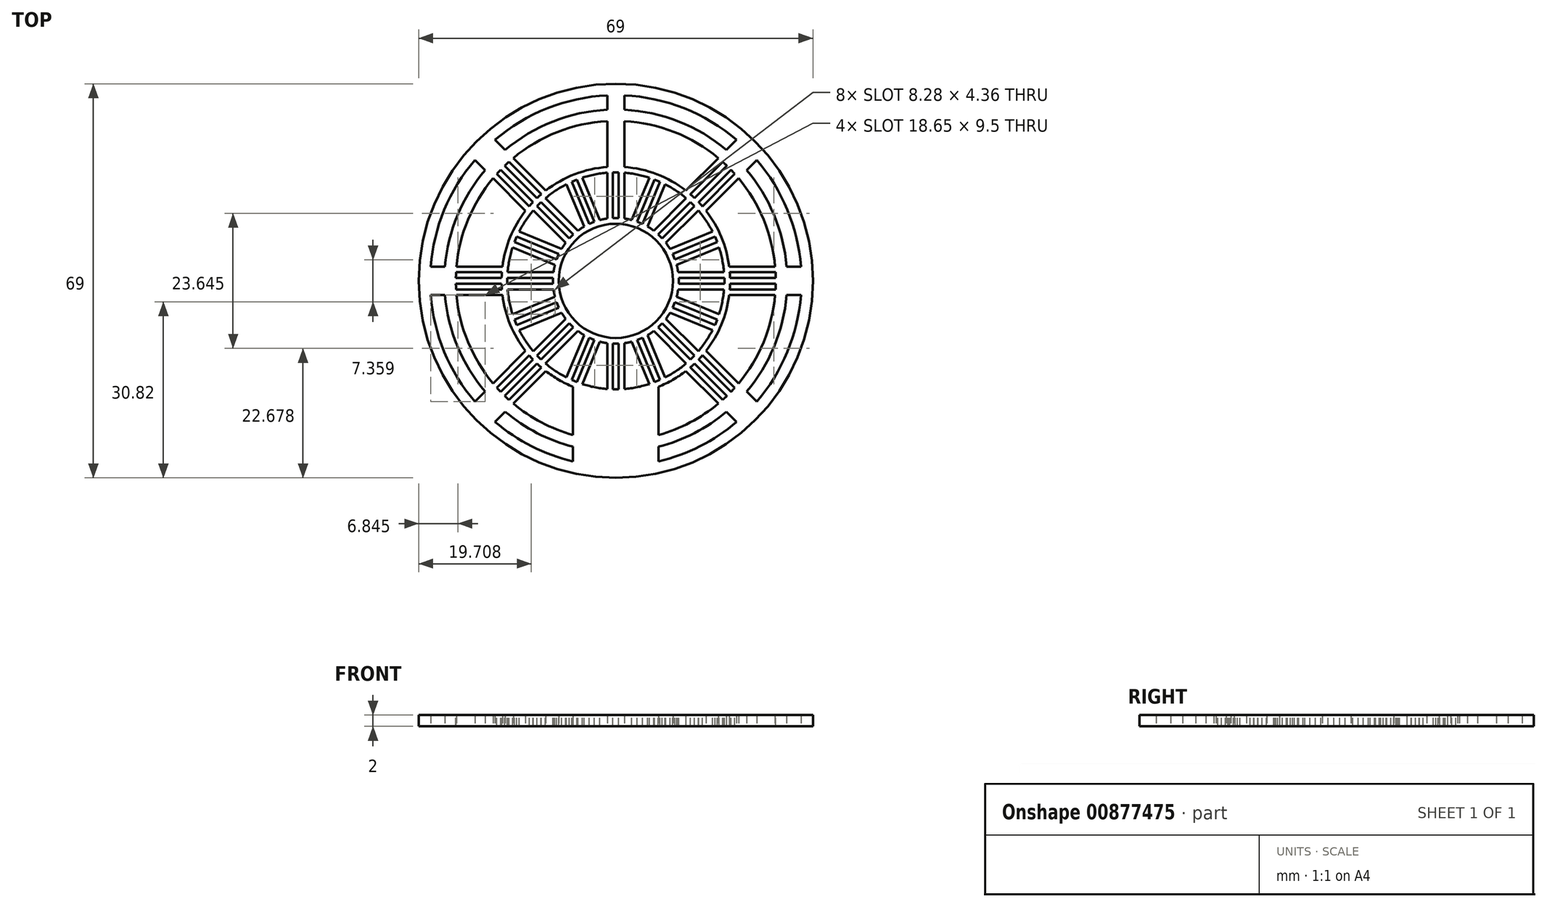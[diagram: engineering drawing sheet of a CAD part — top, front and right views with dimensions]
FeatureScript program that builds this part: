
annotation { "Feature Type Name" : "Feature", "Feature Type Description" : "" }
export const myFeature = defineFeature(function(context is Context, id is Id, definition is map)
    precondition{}
    {
        {
            var Q0;
            Q0=qCreatedBy(makeId("Top.planeOp"),FACE);
            var sketch = newSketch(context, id + "F0", { "sketchPlane" : qUnion([Q0])});
            skLineSegment(sketch, "E0", {"start": v(0, 41.56) * mm, "end": v(0, -42.56) * mm, "construction": true});
            skLineSegment(sketch, "E1", {"start": v(-1.5, 29.96) * mm, "end": v(-1.5, 19.94) * mm});
            skLineSegment(sketch, "E2.MirrorCS", {"start": v(1.5, 29.96) * mm, "end": v(1.5, 19.94) * mm});
            skCircle(sketch, "E3", {"center": v(0, 0) * mm, "radius": 10 * mm});
            skArc(sketch, "E4.trimOffspring", {"start": v(0, 30) * mm, "mid": v(-0.75, 30) * mm, "end": v(-1.5, 29.96) * mm});
            skArc(sketch, "E5", {"start": v(-1.5, 19.94) * mm, "mid": v(-7.19, 18.66) * mm, "end": v(-12.26, 15.8) * mm});
            skArc(sketch, "E6.trimOffspring", {"start": v(7.5, -18.54) * mm, "mid": v(9.98, -17.33) * mm, "end": v(12.26, -15.8) * mm});
            skLineSegment(sketch, "E7", {"start": v(-43.12, 0) * mm, "end": v(49.9, 0) * mm, "construction": true});
            skArc(sketch, "E8.trimOffspring", {"start": v(-19.6, -4) * mm, "mid": v(-18.17, -8.35) * mm, "end": v(-15.8, -12.26) * mm});
            skArc(sketch, "E9.trimOffspring", {"start": v(19.6, 4) * mm, "mid": v(18.17, 8.35) * mm, "end": v(15.8, 12.26) * mm});
            skArc(sketch, "E10", {"start": v(-19.6, 4) * mm, "mid": v(-19.73, 3.25) * mm, "end": v(-19.84, 2.5) * mm});
            skArc(sketch, "E11.trimOffspring", {"start": v(19.6, -4) * mm, "mid": v(19.73, -3.25) * mm, "end": v(19.84, -2.5) * mm});
            skLineSegment(sketch, "E12", {"start": v(-19.84, 2.5) * mm, "end": v(-29.9, 2.5) * mm});
            skLineSegment(sketch, "E13", {"start": v(-19.84, -2.5) * mm, "end": v(-29.9, -2.5) * mm});
            skArc(sketch, "E14.trimOffspring", {"start": v(-19.84, -2.5) * mm, "mid": v(-19.73, -3.25) * mm, "end": v(-19.6, -4) * mm});
            skLineSegment(sketch, "E15.MirrorCS", {"start": v(19.84, 2.5) * mm, "end": v(29.9, 2.5) * mm});
            skLineSegment(sketch, "E16.MirrorCS", {"start": v(19.84, -2.5) * mm, "end": v(29.9, -2.5) * mm});
            skArc(sketch, "E17.trimOffspring", {"start": v(19.84, 2.5) * mm, "mid": v(19.73, 3.25) * mm, "end": v(19.6, 4) * mm});
            skLineSegment(sketch, "E18", {"start": v(-7.5, -18.54) * mm, "end": v(-7.5, -29.05) * mm});
            skLineSegment(sketch, "E19", {"start": v(7.5, -18.54) * mm, "end": v(7.5, -29.05) * mm});
            skArc(sketch, "E20.trimOffspring", {"start": v(1.5, 29.96) * mm, "mid": v(0.75, 30) * mm, "end": v(0, 30) * mm});
            skPoint(sketch, "E21.orphan", {"position": v(29.9, 2.5) * mm});
            skPoint(sketch, "E22.MirrorCS.end.orphan", {"position": v(29.9, -2.5) * mm});
            skArc(sketch, "E23", {"start": v(-19.37, 22.9) * mm, "mid": v(-21.21, 21.21) * mm, "end": v(-22.9, 19.37) * mm});
            skLineSegment(sketch, "E24", {"start": v(-23.88, 23.88) * mm, "end": v(0, 0) * mm, "construction": true});
            skLineSegment(sketch, "E25", {"start": v(-12.26, 15.8) * mm, "end": v(-19.37, 22.9) * mm});
            skLineSegment(sketch, "E26", {"start": v(-15.8, 12.26) * mm, "end": v(-22.9, 19.37) * mm});
            skArc(sketch, "E27.trimOffspring", {"start": v(-29.9, 2.5) * mm, "mid": v(-30, 0) * mm, "end": v(-29.9, -2.5) * mm});
            skArc(sketch, "E28.trimOffspring", {"start": v(-7.5, -29.05) * mm, "mid": v(0, -30) * mm, "end": v(7.5, -29.05) * mm});
            skArc(sketch, "E29.trimOffspring", {"start": v(29.9, -2.5) * mm, "mid": v(30, 0) * mm, "end": v(29.9, 2.5) * mm});
            skArc(sketch, "E30.trimOffspring", {"start": v(1.5, 29.96) * mm, "mid": v(0, 30) * mm, "end": v(-1.5, 29.96) * mm});
            skArc(sketch, "E31.trimOffspring", {"start": v(-15.8, 12.26) * mm, "mid": v(-18.17, 8.35) * mm, "end": v(-19.6, 4) * mm});
            skLineSegment(sketch, "E32.MirrorCS", {"start": v(-15.8, -12.26) * mm, "end": v(-22.9, -19.37) * mm});
            skLineSegment(sketch, "E33.MirrorCS", {"start": v(-12.26, -15.8) * mm, "end": v(-19.37, -22.9) * mm});
            skArc(sketch, "E34.MirrorCS", {"start": v(-19.37, -22.9) * mm, "mid": v(-21.21, -21.21) * mm, "end": v(-22.9, -19.37) * mm});
            skArc(sketch, "E35.MirrorCS", {"start": v(19.37, 22.9) * mm, "mid": v(21.21, 21.21) * mm, "end": v(22.9, 19.37) * mm});
            skLineSegment(sketch, "E36.MirrorCS", {"start": v(12.26, 15.8) * mm, "end": v(19.37, 22.9) * mm});
            skLineSegment(sketch, "E37.MirrorCS", {"start": v(15.8, 12.26) * mm, "end": v(22.9, 19.37) * mm});
            skLineSegment(sketch, "E38.MirrorCS", {"start": v(15.8, -12.26) * mm, "end": v(22.9, -19.37) * mm});
            skArc(sketch, "E39.MirrorCS", {"start": v(19.37, -22.9) * mm, "mid": v(21.21, -21.21) * mm, "end": v(22.9, -19.37) * mm});
            skLineSegment(sketch, "E40.MirrorCS", {"start": v(12.26, -15.8) * mm, "end": v(19.37, -22.9) * mm});
            skArc(sketch, "E41.trimOffspring", {"start": v(12.26, 15.8) * mm, "mid": v(7.19, 18.66) * mm, "end": v(1.5, 19.94) * mm});
            skArc(sketch, "E42.trimOffspring", {"start": v(15.8, -12.26) * mm, "mid": v(18.17, -8.35) * mm, "end": v(19.6, -4) * mm});
            skArc(sketch, "E43.trimOffspring", {"start": v(-12.26, -15.8) * mm, "mid": v(-9.98, -17.33) * mm, "end": v(-7.5, -18.54) * mm});
            skSolve(sketch);
        }
        {
            var Q0;
            Q0=qSketchRegion(id+"F0",true);
            extrude(context, id + "F1", {"entities" : qUnion([Q0]), "depth" : 2 * mm, "offsetDistance" : 25 * mm});
        }
        {
            var Q0;
            Q0=makeQuery(id+"F1.opExtrude","CAP_FACE",FACE,{"disambiguationData":[OSD([sQuery(id+"F0.wireOp",EDGE,"E1"),sQuery(id+"F0.wireOp",EDGE,"E2.MirrorCS"),sQuery(id+"F0.wireOp",EDGE,"AAyOunAg-4wrl-KSGf-zJpX-W6BoPU9CkmaY"),sQuery(id+"F0.wireOp",EDGE,"E3"),sQuery(id+"F0.wireOp",EDGE,"E4.trimOffspring"),sQuery(id+"F0.wireOp",EDGE,"E5"),sQuery(id+"F0.wireOp",EDGE,"c113f9d6-7eb6-46a0-945d-8de39da3101e.trimOffspring"),sQuery(id+"F0.wireOp",EDGE,"3f556c1b-9434-4d6c-9e8b-53cfe23b14e8.trimOffspring"),sQuery(id+"F0.wireOp",EDGE,"E6.trimOffspring"),sQuery(id+"F0.wireOp",EDGE,"E8.trimOffspring"),sQuery(id+"F0.wireOp",EDGE,"E9.trimOffspring"),sQuery(id+"F0.wireOp",EDGE,"E10"),sQuery(id+"F0.wireOp",EDGE,"E11.trimOffspring")])],"isStart":false});
            var sketch = newSketch(context, id + "F2", { "sketchPlane" : qUnion([Q0])});
            skLineSegment(sketch, "E44", {"start": v(0, 19.87) * mm, "end": v(0, -17.42) * mm, "construction": true});
            skLineSegment(sketch, "E45", {"start": v(-0.5, 19) * mm, "end": v(-0.5, 11) * mm});
            skLineSegment(sketch, "E46", {"start": v(-0.5, 11) * mm, "end": v(0, 11) * mm});
            skLineSegment(sketch, "E47", {"start": v(-0.5, 19) * mm, "end": v(0, 19) * mm});
            skCircle(sketch, "E48", {"center": v(0, 0) * mm, "radius": 15 * mm, "construction": true});
            skLineSegment(sketch, "E49.MirrorCS", {"start": v(0.5, 19) * mm, "end": v(0, 19) * mm});
            skLineSegment(sketch, "E50.MirrorCS", {"start": v(0.5, 19) * mm, "end": v(0.5, 11) * mm});
            skLineSegment(sketch, "E51.MirrorCS", {"start": v(0.5, 11) * mm, "end": v(0, 11) * mm});
            skLineSegment(sketch, "E52.1.0", {"start": v(7.73, 17.36) * mm, "end": v(7.27, 17.55) * mm});
            skLineSegment(sketch, "E52.1.1", {"start": v(7.73, 17.36) * mm, "end": v(4.67, 9.97) * mm});
            skLineSegment(sketch, "E52.1.2", {"start": v(6.8, 17.75) * mm, "end": v(7.27, 17.55) * mm});
            skLineSegment(sketch, "E52.1.3", {"start": v(6.8, 17.75) * mm, "end": v(3.75, 10.35) * mm});
            skLineSegment(sketch, "E52.1.4", {"start": v(3.75, 10.35) * mm, "end": v(4.2, 10.16) * mm});
            skLineSegment(sketch, "E52.1.5", {"start": v(4.67, 9.97) * mm, "end": v(4.2, 10.16) * mm});
            skLineSegment(sketch, "E52.2.0", {"start": v(13.79, 13.08) * mm, "end": v(13.44, 13.44) * mm});
            skLineSegment(sketch, "E52.2.1", {"start": v(13.79, 13.08) * mm, "end": v(8.13, 7.42) * mm});
            skLineSegment(sketch, "E52.2.2", {"start": v(13.08, 13.79) * mm, "end": v(13.44, 13.44) * mm});
            skLineSegment(sketch, "E52.2.3", {"start": v(13.08, 13.79) * mm, "end": v(7.42, 8.13) * mm});
            skLineSegment(sketch, "E52.2.4", {"start": v(7.42, 8.13) * mm, "end": v(7.78, 7.78) * mm});
            skLineSegment(sketch, "E52.2.5", {"start": v(8.13, 7.42) * mm, "end": v(7.78, 7.78) * mm});
            skLineSegment(sketch, "E52.3.0", {"start": v(17.75, 6.8) * mm, "end": v(17.55, 7.27) * mm});
            skLineSegment(sketch, "E52.3.1", {"start": v(17.75, 6.8) * mm, "end": v(10.35, 3.75) * mm});
            skLineSegment(sketch, "E52.3.2", {"start": v(17.36, 7.73) * mm, "end": v(17.55, 7.27) * mm});
            skLineSegment(sketch, "E52.3.3", {"start": v(17.36, 7.73) * mm, "end": v(9.97, 4.67) * mm});
            skLineSegment(sketch, "E52.3.4", {"start": v(9.97, 4.67) * mm, "end": v(10.16, 4.2) * mm});
            skLineSegment(sketch, "E52.3.5", {"start": v(10.35, 3.75) * mm, "end": v(10.16, 4.2) * mm});
            skLineSegment(sketch, "E52.4.0", {"start": v(19, -0.5) * mm, "end": v(19, 0) * mm});
            skLineSegment(sketch, "E52.4.1", {"start": v(19, -0.5) * mm, "end": v(11, -0.5) * mm});
            skLineSegment(sketch, "E52.4.2", {"start": v(19, 0.5) * mm, "end": v(19, 0) * mm});
            skLineSegment(sketch, "E52.4.3", {"start": v(19, 0.5) * mm, "end": v(11, 0.5) * mm});
            skLineSegment(sketch, "E52.4.4", {"start": v(11, 0.5) * mm, "end": v(11, 0) * mm});
            skLineSegment(sketch, "E52.4.5", {"start": v(11, -0.5) * mm, "end": v(11, 0) * mm});
            skLineSegment(sketch, "E52.5.0", {"start": v(17.36, -7.73) * mm, "end": v(17.55, -7.27) * mm});
            skLineSegment(sketch, "E52.5.1", {"start": v(17.36, -7.73) * mm, "end": v(9.97, -4.67) * mm});
            skLineSegment(sketch, "E52.5.2", {"start": v(17.75, -6.8) * mm, "end": v(17.55, -7.27) * mm});
            skLineSegment(sketch, "E52.5.3", {"start": v(17.75, -6.8) * mm, "end": v(10.35, -3.75) * mm});
            skLineSegment(sketch, "E52.5.4", {"start": v(10.35, -3.75) * mm, "end": v(10.16, -4.2) * mm});
            skLineSegment(sketch, "E52.5.5", {"start": v(9.97, -4.67) * mm, "end": v(10.16, -4.2) * mm});
            skLineSegment(sketch, "E52.6.0", {"start": v(13.08, -13.79) * mm, "end": v(13.44, -13.44) * mm});
            skLineSegment(sketch, "E52.6.1", {"start": v(13.08, -13.79) * mm, "end": v(7.42, -8.13) * mm});
            skLineSegment(sketch, "E52.6.2", {"start": v(13.79, -13.08) * mm, "end": v(13.44, -13.44) * mm});
            skLineSegment(sketch, "E52.6.3", {"start": v(13.79, -13.08) * mm, "end": v(8.13, -7.42) * mm});
            skLineSegment(sketch, "E52.6.4", {"start": v(8.13, -7.42) * mm, "end": v(7.78, -7.78) * mm});
            skLineSegment(sketch, "E52.6.5", {"start": v(7.42, -8.13) * mm, "end": v(7.78, -7.78) * mm});
            skLineSegment(sketch, "E52.7.0", {"start": v(6.8, -17.75) * mm, "end": v(7.27, -17.55) * mm});
            skLineSegment(sketch, "E52.7.1", {"start": v(6.8, -17.75) * mm, "end": v(3.75, -10.35) * mm});
            skLineSegment(sketch, "E52.7.2", {"start": v(7.73, -17.36) * mm, "end": v(7.27, -17.55) * mm});
            skLineSegment(sketch, "E52.7.3", {"start": v(7.73, -17.36) * mm, "end": v(4.67, -9.97) * mm});
            skLineSegment(sketch, "E52.7.4", {"start": v(4.67, -9.97) * mm, "end": v(4.2, -10.16) * mm});
            skLineSegment(sketch, "E52.7.5", {"start": v(3.75, -10.35) * mm, "end": v(4.2, -10.16) * mm});
            skLineSegment(sketch, "E52.8.0", {"start": v(-0.5, -19) * mm, "end": v(0, -19) * mm});
            skLineSegment(sketch, "E52.8.1", {"start": v(-0.5, -19) * mm, "end": v(-0.5, -11) * mm});
            skLineSegment(sketch, "E52.8.2", {"start": v(0.5, -19) * mm, "end": v(0, -19) * mm});
            skLineSegment(sketch, "E52.8.3", {"start": v(0.5, -19) * mm, "end": v(0.5, -11) * mm});
            skLineSegment(sketch, "E52.8.4", {"start": v(0.5, -11) * mm, "end": v(0, -11) * mm});
            skLineSegment(sketch, "E52.8.5", {"start": v(-0.5, -11) * mm, "end": v(0, -11) * mm});
            skLineSegment(sketch, "E52.anchor1", {"start": v(0, 0) * mm, "end": v(0, 19) * mm, "construction": true});
            skLineSegment(sketch, "E52.anchor2", {"start": v(0, 0) * mm, "end": v(0, -19) * mm, "construction": true});
            skLineSegment(sketch, "E53.MirrorCS", {"start": v(-13.79, 13.08) * mm, "end": v(-13.44, 13.44) * mm});
            skLineSegment(sketch, "E54.MirrorCS", {"start": v(-19, 0.5) * mm, "end": v(-19, 0) * mm});
            skLineSegment(sketch, "E55.MirrorCS", {"start": v(-7.42, 8.13) * mm, "end": v(-7.78, 7.78) * mm});
            skLineSegment(sketch, "E56.MirrorCS", {"start": v(-17.75, -6.8) * mm, "end": v(-17.55, -7.27) * mm});
            skLineSegment(sketch, "E57.MirrorCS", {"start": v(-13.08, 13.79) * mm, "end": v(-13.44, 13.44) * mm});
            skLineSegment(sketch, "E58.MirrorCS", {"start": v(-8.13, -7.42) * mm, "end": v(-7.78, -7.78) * mm});
            skLineSegment(sketch, "E59.MirrorCS", {"start": v(-13.79, -13.08) * mm, "end": v(-13.44, -13.44) * mm});
            skLineSegment(sketch, "E60.MirrorCS", {"start": v(-17.75, 6.8) * mm, "end": v(-17.55, 7.27) * mm});
            skLineSegment(sketch, "E61.MirrorCS", {"start": v(-19, -0.5) * mm, "end": v(-19, 0) * mm});
            skLineSegment(sketch, "E62.MirrorCS", {"start": v(-13.08, -13.79) * mm, "end": v(-13.44, -13.44) * mm});
            skLineSegment(sketch, "E63.MirrorCS", {"start": v(-11, 0.5) * mm, "end": v(-11, 0) * mm});
            skLineSegment(sketch, "E64.MirrorCS", {"start": v(-6.8, -17.75) * mm, "end": v(-7.27, -17.55) * mm});
            skLineSegment(sketch, "E65.MirrorCS", {"start": v(-10.35, -3.75) * mm, "end": v(-10.16, -4.2) * mm});
            skLineSegment(sketch, "E66.MirrorCS", {"start": v(-7.73, 17.36) * mm, "end": v(-7.27, 17.55) * mm});
            skLineSegment(sketch, "E67.MirrorCS", {"start": v(-9.97, 4.67) * mm, "end": v(-10.16, 4.2) * mm});
            skLineSegment(sketch, "E68.MirrorCS", {"start": v(-9.97, -4.67) * mm, "end": v(-10.16, -4.2) * mm});
            skLineSegment(sketch, "E69.MirrorCS", {"start": v(-10.35, 3.75) * mm, "end": v(-10.16, 4.2) * mm});
            skLineSegment(sketch, "E70.MirrorCS", {"start": v(-7.73, -17.36) * mm, "end": v(-7.27, -17.55) * mm});
            skLineSegment(sketch, "E71.MirrorCS", {"start": v(-8.13, 7.42) * mm, "end": v(-7.78, 7.78) * mm});
            skLineSegment(sketch, "E72.MirrorCS", {"start": v(-7.42, -8.13) * mm, "end": v(-7.78, -7.78) * mm});
            skLineSegment(sketch, "E73.MirrorCS", {"start": v(-17.36, 7.73) * mm, "end": v(-17.55, 7.27) * mm});
            skLineSegment(sketch, "E74.MirrorCS", {"start": v(-11, -0.5) * mm, "end": v(-11, 0) * mm});
            skLineSegment(sketch, "E75.MirrorCS", {"start": v(-6.8, 17.75) * mm, "end": v(-7.27, 17.55) * mm});
            skLineSegment(sketch, "E76.MirrorCS", {"start": v(-17.36, -7.73) * mm, "end": v(-17.55, -7.27) * mm});
            skLineSegment(sketch, "E77.MirrorCS", {"start": v(-17.36, 7.73) * mm, "end": v(-9.97, 4.67) * mm});
            skLineSegment(sketch, "E78.MirrorCS", {"start": v(-13.79, -13.08) * mm, "end": v(-8.13, -7.42) * mm});
            skLineSegment(sketch, "E79.MirrorCS", {"start": v(-17.75, -6.8) * mm, "end": v(-10.35, -3.75) * mm});
            skLineSegment(sketch, "E80.MirrorCS", {"start": v(-19, 0.5) * mm, "end": v(-11, 0.5) * mm});
            skLineSegment(sketch, "E81.MirrorCS", {"start": v(-7.73, -17.36) * mm, "end": v(-4.67, -9.97) * mm});
            skLineSegment(sketch, "E82.MirrorCS", {"start": v(-17.75, 6.8) * mm, "end": v(-10.35, 3.75) * mm});
            skLineSegment(sketch, "E83.MirrorCS", {"start": v(-17.36, -7.73) * mm, "end": v(-9.97, -4.67) * mm});
            skLineSegment(sketch, "E84.MirrorCS", {"start": v(-7.73, 17.36) * mm, "end": v(-4.67, 9.97) * mm});
            skLineSegment(sketch, "E85.MirrorCS", {"start": v(-13.08, 13.79) * mm, "end": v(-7.42, 8.13) * mm});
            skLineSegment(sketch, "E86.MirrorCS", {"start": v(-19, -0.5) * mm, "end": v(-11, -0.5) * mm});
            skLineSegment(sketch, "E87.MirrorCS", {"start": v(-13.79, 13.08) * mm, "end": v(-8.13, 7.42) * mm});
            skLineSegment(sketch, "E88.MirrorCS", {"start": v(-13.08, -13.79) * mm, "end": v(-7.42, -8.13) * mm});
            skLineSegment(sketch, "E89.MirrorCS", {"start": v(-6.8, 17.75) * mm, "end": v(-3.75, 10.35) * mm});
            skLineSegment(sketch, "E90.MirrorCS", {"start": v(-3.75, 10.35) * mm, "end": v(-4.2, 10.16) * mm});
            skLineSegment(sketch, "E91.MirrorCS", {"start": v(-4.67, 9.97) * mm, "end": v(-4.2, 10.16) * mm});
            skLineSegment(sketch, "E92.MirrorCS", {"start": v(-3.75, -10.35) * mm, "end": v(-4.2, -10.16) * mm});
            skLineSegment(sketch, "E93.MirrorCS", {"start": v(-4.67, -9.97) * mm, "end": v(-4.2, -10.16) * mm});
            skLineSegment(sketch, "E94.MirrorCS", {"start": v(-6.8, -17.75) * mm, "end": v(-3.75, -10.35) * mm});
            skSolve(sketch);
        }
        {
            var Q0;
            Q0=qSketchRegion(id+"F2",true);
            extrude(context, id + "F3", {"entities" : qUnion([Q0]), "operationType" : NewBodyOperationType.REMOVE, "oppositeDirection" : true, "depth" : 25 * mm, "offsetDistance" : 25 * mm});
        }
        {
            var Q0;
            Q0=makeQuery(id+"F1.opExtrude","CAP_FACE",FACE,{"disambiguationData":[OSD([sQuery(id+"F0.wireOp",EDGE,"E1"),sQuery(id+"F0.wireOp",EDGE,"E2.MirrorCS"),sQuery(id+"F0.wireOp",EDGE,"AAyOunAg-4wrl-KSGf-zJpX-W6BoPU9CkmaY"),sQuery(id+"F0.wireOp",EDGE,"E3"),sQuery(id+"F0.wireOp",EDGE,"E4.trimOffspring"),sQuery(id+"F0.wireOp",EDGE,"E5"),sQuery(id+"F0.wireOp",EDGE,"c113f9d6-7eb6-46a0-945d-8de39da3101e.trimOffspring"),sQuery(id+"F0.wireOp",EDGE,"3f556c1b-9434-4d6c-9e8b-53cfe23b14e8.trimOffspring"),sQuery(id+"F0.wireOp",EDGE,"E6.trimOffspring"),sQuery(id+"F0.wireOp",EDGE,"E8.trimOffspring"),sQuery(id+"F0.wireOp",EDGE,"E9.trimOffspring"),sQuery(id+"F0.wireOp",EDGE,"E10"),sQuery(id+"F0.wireOp",EDGE,"E11.trimOffspring")])],"isStart":false});
            var sketch = newSketch(context, id + "F4", { "sketchPlane" : qUnion([Q0])});
            skArc(sketch, "E95", {"start": v(-1.5, 10.9) * mm, "mid": v(-2.15, 10.8) * mm, "end": v(-2.79, 10.65) * mm});
            skLineSegment(sketch, "E96", {"start": v(-1.5, 10.9) * mm, "end": v(-1.5, 18.93) * mm});
            skLineSegment(sketch, "E97", {"start": v(-2.79, 10.65) * mm, "end": v(-5.86, 18.07) * mm});
            skArc(sketch, "E98", {"start": v(-1.5, 18.93) * mm, "mid": v(-3.7, 18.63) * mm, "end": v(-5.86, 18.07) * mm});
            skArc(sketch, "E99.1.0", {"start": v(5.86, 18.07) * mm, "mid": v(3.7, 18.63) * mm, "end": v(1.5, 18.93) * mm});
            skLineSegment(sketch, "E99.1.1", {"start": v(2.79, 10.65) * mm, "end": v(5.86, 18.07) * mm});
            skArc(sketch, "E99.1.2", {"start": v(2.79, 10.65) * mm, "mid": v(2.15, 10.8) * mm, "end": v(1.5, 10.9) * mm});
            skLineSegment(sketch, "E99.1.3", {"start": v(1.5, 10.9) * mm, "end": v(1.5, 18.93) * mm});
            skArc(sketch, "E99.2.0", {"start": v(12.33, 14.45) * mm, "mid": v(10.55, 15.8) * mm, "end": v(8.63, 16.92) * mm});
            skLineSegment(sketch, "E99.2.1", {"start": v(6.65, 8.77) * mm, "end": v(12.33, 14.45) * mm});
            skArc(sketch, "E99.2.2", {"start": v(6.65, 8.77) * mm, "mid": v(6.12, 9.16) * mm, "end": v(5.56, 9.5) * mm});
            skLineSegment(sketch, "E99.2.3", {"start": v(5.56, 9.5) * mm, "end": v(8.63, 16.92) * mm});
            skArc(sketch, "E99.3.0", {"start": v(16.92, 8.63) * mm, "mid": v(15.8, 10.55) * mm, "end": v(14.45, 12.33) * mm});
            skLineSegment(sketch, "E99.3.1", {"start": v(9.5, 5.56) * mm, "end": v(16.92, 8.63) * mm});
            skArc(sketch, "E99.3.2", {"start": v(9.5, 5.56) * mm, "mid": v(9.16, 6.12) * mm, "end": v(8.77, 6.65) * mm});
            skLineSegment(sketch, "E99.3.3", {"start": v(8.77, 6.65) * mm, "end": v(14.45, 12.33) * mm});
            skArc(sketch, "E99.4.0", {"start": v(18.93, 1.5) * mm, "mid": v(18.63, 3.7) * mm, "end": v(18.07, 5.86) * mm});
            skLineSegment(sketch, "E99.4.1", {"start": v(10.9, 1.5) * mm, "end": v(18.93, 1.5) * mm});
            skArc(sketch, "E99.4.2", {"start": v(10.9, 1.5) * mm, "mid": v(10.8, 2.15) * mm, "end": v(10.65, 2.79) * mm});
            skLineSegment(sketch, "E99.4.3", {"start": v(10.65, 2.79) * mm, "end": v(18.07, 5.86) * mm});
            skArc(sketch, "E99.5.0", {"start": v(18.07, -5.86) * mm, "mid": v(18.63, -3.7) * mm, "end": v(18.93, -1.5) * mm});
            skLineSegment(sketch, "E99.5.1", {"start": v(10.65, -2.79) * mm, "end": v(18.07, -5.86) * mm});
            skArc(sketch, "E99.5.2", {"start": v(10.65, -2.79) * mm, "mid": v(10.8, -2.15) * mm, "end": v(10.9, -1.5) * mm});
            skLineSegment(sketch, "E99.5.3", {"start": v(10.9, -1.5) * mm, "end": v(18.93, -1.5) * mm});
            skArc(sketch, "E99.6.0", {"start": v(14.45, -12.33) * mm, "mid": v(15.8, -10.55) * mm, "end": v(16.92, -8.63) * mm});
            skLineSegment(sketch, "E99.6.1", {"start": v(8.77, -6.65) * mm, "end": v(14.45, -12.33) * mm});
            skArc(sketch, "E99.6.2", {"start": v(8.77, -6.65) * mm, "mid": v(9.16, -6.12) * mm, "end": v(9.5, -5.56) * mm});
            skLineSegment(sketch, "E99.6.3", {"start": v(9.5, -5.56) * mm, "end": v(16.92, -8.63) * mm});
            skArc(sketch, "E99.7.0", {"start": v(8.63, -16.92) * mm, "mid": v(10.55, -15.8) * mm, "end": v(12.33, -14.45) * mm});
            skLineSegment(sketch, "E99.7.1", {"start": v(5.56, -9.5) * mm, "end": v(8.63, -16.92) * mm});
            skArc(sketch, "E99.7.2", {"start": v(5.56, -9.5) * mm, "mid": v(6.12, -9.16) * mm, "end": v(6.65, -8.77) * mm});
            skLineSegment(sketch, "E99.7.3", {"start": v(6.65, -8.77) * mm, "end": v(12.33, -14.45) * mm});
            skArc(sketch, "E99.8.0", {"start": v(1.5, -18.93) * mm, "mid": v(3.7, -18.63) * mm, "end": v(5.86, -18.07) * mm});
            skLineSegment(sketch, "E99.8.1", {"start": v(1.5, -10.9) * mm, "end": v(1.5, -18.93) * mm});
            skArc(sketch, "E99.8.2", {"start": v(1.5, -10.9) * mm, "mid": v(2.15, -10.8) * mm, "end": v(2.79, -10.65) * mm});
            skLineSegment(sketch, "E99.8.3", {"start": v(2.79, -10.65) * mm, "end": v(5.86, -18.07) * mm});
            skLineSegment(sketch, "E99.anchor1", {"start": v(0, 0) * mm, "end": v(-5.86, 18.07) * mm, "construction": true});
            skLineSegment(sketch, "E99.anchor2", {"start": v(0, 0) * mm, "end": v(5.86, -18.07) * mm, "construction": true});
            skLineSegment(sketch, "E100", {"start": v(0, 24.57) * mm, "end": v(0, -24.9) * mm, "construction": true});
            skPoint(sketch, "E100.startSnap0", {"position": v(0, 23.23) * mm});
            skArc(sketch, "E101.MirrorCS", {"start": v(-12.33, 14.45) * mm, "mid": v(-10.55, 15.8) * mm, "end": v(-8.63, 16.92) * mm});
            skArc(sketch, "E102.MirrorCS", {"start": v(-10.9, 1.5) * mm, "mid": v(-10.8, 2.15) * mm, "end": v(-10.65, 2.79) * mm});
            skArc(sketch, "E103.MirrorCS", {"start": v(-8.77, -6.65) * mm, "mid": v(-9.16, -6.12) * mm, "end": v(-9.5, -5.56) * mm});
            skArc(sketch, "E104.MirrorCS", {"start": v(-10.65, -2.79) * mm, "mid": v(-10.8, -2.15) * mm, "end": v(-10.9, -1.5) * mm});
            skArc(sketch, "E105.MirrorCS", {"start": v(-9.5, 5.56) * mm, "mid": v(-9.16, 6.12) * mm, "end": v(-8.77, 6.65) * mm});
            skLineSegment(sketch, "E106.MirrorCS", {"start": v(-10.9, 1.5) * mm, "end": v(-18.93, 1.5) * mm});
            skLineSegment(sketch, "E107.MirrorCS", {"start": v(-8.77, -6.65) * mm, "end": v(-14.45, -12.33) * mm});
            skLineSegment(sketch, "E108.MirrorCS", {"start": v(-9.5, -5.56) * mm, "end": v(-16.92, -8.63) * mm});
            skArc(sketch, "E109.MirrorCS", {"start": v(-8.63, -16.92) * mm, "mid": v(-10.55, -15.8) * mm, "end": v(-12.33, -14.45) * mm});
            skArc(sketch, "E110.MirrorCS", {"start": v(-16.92, 8.63) * mm, "mid": v(-15.8, 10.55) * mm, "end": v(-14.45, 12.33) * mm});
            skLineSegment(sketch, "E111.MirrorCS", {"start": v(-10.65, -2.79) * mm, "end": v(-18.07, -5.86) * mm});
            skArc(sketch, "E112.MirrorCS", {"start": v(-14.45, -12.33) * mm, "mid": v(-15.8, -10.55) * mm, "end": v(-16.92, -8.63) * mm});
            skArc(sketch, "E113.MirrorCS", {"start": v(-18.93, 1.5) * mm, "mid": v(-18.63, 3.7) * mm, "end": v(-18.07, 5.86) * mm});
            skLineSegment(sketch, "E114.MirrorCS", {"start": v(-8.77, 6.65) * mm, "end": v(-14.45, 12.33) * mm});
            skLineSegment(sketch, "E115.MirrorCS", {"start": v(-10.65, 2.79) * mm, "end": v(-18.07, 5.86) * mm});
            skLineSegment(sketch, "E116.MirrorCS", {"start": v(-10.9, -1.5) * mm, "end": v(-18.93, -1.5) * mm});
            skLineSegment(sketch, "E117.MirrorCS", {"start": v(-9.5, 5.56) * mm, "end": v(-16.92, 8.63) * mm});
            skArc(sketch, "E118.MirrorCS", {"start": v(-18.07, -5.86) * mm, "mid": v(-18.63, -3.7) * mm, "end": v(-18.93, -1.5) * mm});
            skLineSegment(sketch, "E119.MirrorCS", {"start": v(-5.56, 9.5) * mm, "end": v(-8.63, 16.92) * mm});
            skLineSegment(sketch, "E120.MirrorCS", {"start": v(-6.65, 8.77) * mm, "end": v(-12.33, 14.45) * mm});
            skArc(sketch, "E121.MirrorCS", {"start": v(-6.65, 8.77) * mm, "mid": v(-6.12, 9.16) * mm, "end": v(-5.56, 9.5) * mm});
            skArc(sketch, "E122.MirrorCS", {"start": v(-5.56, -9.5) * mm, "mid": v(-6.12, -9.16) * mm, "end": v(-6.65, -8.77) * mm});
            skLineSegment(sketch, "E123.MirrorCS", {"start": v(-6.65, -8.77) * mm, "end": v(-12.33, -14.45) * mm});
            skLineSegment(sketch, "E124.MirrorCS", {"start": v(-5.56, -9.5) * mm, "end": v(-8.63, -16.92) * mm});
            skLineSegment(sketch, "E125.MirrorCS", {"start": v(-2.79, -10.65) * mm, "end": v(-5.86, -18.07) * mm});
            skArc(sketch, "E126.MirrorCS", {"start": v(-1.5, -10.9) * mm, "mid": v(-2.15, -10.8) * mm, "end": v(-2.79, -10.65) * mm});
            skLineSegment(sketch, "E127.MirrorCS", {"start": v(-1.5, -10.9) * mm, "end": v(-1.5, -18.93) * mm});
            skArc(sketch, "E128.MirrorCS", {"start": v(-1.5, -18.93) * mm, "mid": v(-3.7, -18.63) * mm, "end": v(-5.86, -18.07) * mm});
            skSolve(sketch);
        }
        {
            var Q0;
            Q0=qSketchRegion(id+"F4",true);
            extrude(context, id + "F5", {"entities" : qUnion([Q0]), "operationType" : NewBodyOperationType.REMOVE, "oppositeDirection" : true, "depth" : 25 * mm, "offsetDistance" : 25 * mm});
        }
        {
            var Q0;
            Q0=qCreatedBy(makeId("Top.planeOp"),FACE);
            var sketch = newSketch(context, id + "F6", { "sketchPlane" : qUnion([Q0])});
            skCircle(sketch, "E129", {"center": v(0, 0) * mm, "radius": 30 * mm});
            skCircle(sketch, "E130.0", {"center": v(0, 0) * mm, "radius": 28 * mm});
            skSolve(sketch);
        }
        {
            var Q0;
            Q0=qSketchRegion(id+"F6",true);
            extrude(context, id + "F7", {"entities" : qUnion([Q0]), "operationType" : NewBodyOperationType.ADD, "depth" : 2 * mm, "offsetDistance" : 25 * mm});
        }
        {
            var Q0;
            Q0=makeQuery(id+"F7.boolean.opBoolean","MERGE",FACE,{"derivedFrom":[makeQuery(id+"F1.opExtrude","CAP_FACE",FACE,{"disambiguationData":[OSD([sQuery(id+"F0.wireOp",EDGE,"E1"),sQuery(id+"F0.wireOp",EDGE,"E2.MirrorCS"),sQuery(id+"F0.wireOp",EDGE,"AAyOunAg-4wrl-KSGf-zJpX-W6BoPU9CkmaY"),sQuery(id+"F0.wireOp",EDGE,"E3"),sQuery(id+"F0.wireOp",EDGE,"E4.trimOffspring"),sQuery(id+"F0.wireOp",EDGE,"E5"),sQuery(id+"F0.wireOp",EDGE,"c113f9d6-7eb6-46a0-945d-8de39da3101e.trimOffspring"),sQuery(id+"F0.wireOp",EDGE,"3f556c1b-9434-4d6c-9e8b-53cfe23b14e8.trimOffspring"),sQuery(id+"F0.wireOp",EDGE,"E6.trimOffspring"),sQuery(id+"F0.wireOp",EDGE,"E8.trimOffspring"),sQuery(id+"F0.wireOp",EDGE,"E9.trimOffspring"),sQuery(id+"F0.wireOp",EDGE,"E10"),sQuery(id+"F0.wireOp",EDGE,"E11.trimOffspring"),sQuery(id+"F0.wireOp",EDGE,"E12"),sQuery(id+"F0.wireOp",EDGE,"kXOEPWS2-C3rD-1ilS-GXDP-zmpu0qmiIk17"),sQuery(id+"F0.wireOp",EDGE,"ba19601d-0a29-4faa-a46e-a923055b0abc.trimOffspring"),sQuery(id+"F0.wireOp",EDGE,"E13"),sQuery(id+"F0.wireOp",EDGE,"E14.trimOffspring"),sQuery(id+"F0.wireOp",EDGE,"E15.MirrorCS"),sQuery(id+"F0.wireOp",EDGE,"E22.MirrorCS"),sQuery(id+"F0.wireOp",EDGE,"E16.MirrorCS"),sQuery(id+"F0.wireOp",EDGE,"E17.trimOffspring")])],"isStart":false}),makeQuery(id+"F7.opExtrude","CAP_FACE",FACE,{"disambiguationData":[OSD([sQuery(id+"F6.wireOp",EDGE,"E129"),sQuery(id+"F6.wireOp",EDGE,"E130.0")])],"isStart":false})]});
            var sketch = newSketch(context, id + "F8", { "sketchPlane" : qUnion([Q0])});
            skLineSegment(sketch, "E131.1.0", {"start": v(-19.94, 1.5) * mm, "end": v(-27.96, 1.5) * mm});
            skLineSegment(sketch, "E131.1.1", {"start": v(-20, 0.5) * mm, "end": v(-28, 0.5) * mm});
            skArc(sketch, "E131.1.2", {"start": v(-20, -0.5) * mm, "mid": v(-19.97, -1) * mm, "end": v(-19.94, -1.5) * mm});
            skArc(sketch, "E131.1.3", {"start": v(-28, -0.5) * mm, "mid": v(-27.98, -1) * mm, "end": v(-27.96, -1.5) * mm});
            skLineSegment(sketch, "E131.1.4", {"start": v(-20, -0.5) * mm, "end": v(-28, -0.5) * mm});
            skArc(sketch, "E131.1.5", {"start": v(-19.94, 1.5) * mm, "mid": v(-19.97, 1) * mm, "end": v(-20, 0.5) * mm});
            skPoint(sketch, "E131.1.6", {"position": v(-19.94, 1.5) * mm});
            skLineSegment(sketch, "E131.1.7", {"start": v(-19.94, -1.5) * mm, "end": v(-27.96, -1.5) * mm});
            skArc(sketch, "E131.1.8", {"start": v(-27.96, 1.5) * mm, "mid": v(-27.98, 1) * mm, "end": v(-28, 0.5) * mm});
            skPoint(sketch, "E131.center", {"position": v(0, 0) * mm});
            skLineSegment(sketch, "E132", {"start": v(0, -35.42) * mm, "end": v(0, 33.86) * mm, "construction": true});
            skArc(sketch, "E133.MirrorCS", {"start": v(19.94, 1.5) * mm, "mid": v(19.97, 1) * mm, "end": v(20, 0.5) * mm});
            skArc(sketch, "E134.MirrorCS", {"start": v(20, -0.5) * mm, "mid": v(19.97, -1) * mm, "end": v(19.94, -1.5) * mm});
            skArc(sketch, "E135.MirrorCS", {"start": v(27.96, 1.5) * mm, "mid": v(27.98, 1) * mm, "end": v(28, 0.5) * mm});
            skArc(sketch, "E136.MirrorCS", {"start": v(28, -0.5) * mm, "mid": v(27.98, -1) * mm, "end": v(27.96, -1.5) * mm});
            skPoint(sketch, "E137.MirrorP", {"position": v(19.94, 1.5) * mm});
            skLineSegment(sketch, "E138.MirrorCS", {"start": v(19.94, 1.5) * mm, "end": v(27.96, 1.5) * mm});
            skLineSegment(sketch, "E139.MirrorCS", {"start": v(19.94, -1.5) * mm, "end": v(27.96, -1.5) * mm});
            skLineSegment(sketch, "E140.MirrorCS", {"start": v(20, -0.5) * mm, "end": v(28, -0.5) * mm});
            skLineSegment(sketch, "E141.MirrorCS", {"start": v(20, 0.5) * mm, "end": v(28, 0.5) * mm});
            skLineSegment(sketch, "E142.1.0", {"start": v(-14.5, 13.78) * mm, "end": v(-20.15, 19.44) * mm});
            skLineSegment(sketch, "E142.1.1", {"start": v(-13.04, 15.16) * mm, "end": v(-18.7, 20.83) * mm});
            skPoint(sketch, "E142.1.2", {"position": v(-13.04, 15.16) * mm});
            skLineSegment(sketch, "E142.1.3", {"start": v(-13.78, 14.5) * mm, "end": v(-19.44, 20.15) * mm});
            skLineSegment(sketch, "E142.1.4", {"start": v(-15.16, 13.04) * mm, "end": v(-20.83, 18.7) * mm});
            skArc(sketch, "E142.1.5", {"start": v(-18.7, 20.83) * mm, "mid": v(-19.08, 20.5) * mm, "end": v(-19.44, 20.15) * mm});
            skArc(sketch, "E142.1.6", {"start": v(-20.15, 19.44) * mm, "mid": v(-20.5, 19.08) * mm, "end": v(-20.83, 18.7) * mm});
            skArc(sketch, "E142.1.7", {"start": v(-13.04, 15.16) * mm, "mid": v(-13.42, 14.83) * mm, "end": v(-13.78, 14.5) * mm});
            skArc(sketch, "E142.1.8", {"start": v(-14.5, 13.78) * mm, "mid": v(-14.83, 13.42) * mm, "end": v(-15.16, 13.04) * mm});
            skLineSegment(sketch, "E143", {"start": v(-33.35, 0) * mm, "end": v(38.88, 0) * mm, "construction": true});
            skArc(sketch, "E144.MirrorCS", {"start": v(-13.04, -15.16) * mm, "mid": v(-13.42, -14.83) * mm, "end": v(-13.78, -14.5) * mm});
            skArc(sketch, "E145.MirrorCS", {"start": v(-14.5, -13.78) * mm, "mid": v(-14.83, -13.42) * mm, "end": v(-15.16, -13.04) * mm});
            skArc(sketch, "E146.MirrorCS", {"start": v(-20.15, -19.44) * mm, "mid": v(-20.5, -19.08) * mm, "end": v(-20.83, -18.7) * mm});
            skArc(sketch, "E147.MirrorCS", {"start": v(-18.7, -20.83) * mm, "mid": v(-19.08, -20.5) * mm, "end": v(-19.44, -20.15) * mm});
            skPoint(sketch, "E148.MirrorP", {"position": v(-13.04, -15.16) * mm});
            skLineSegment(sketch, "E149.MirrorCS", {"start": v(-13.78, -14.5) * mm, "end": v(-19.44, -20.15) * mm});
            skLineSegment(sketch, "E150.MirrorCS", {"start": v(-15.16, -13.04) * mm, "end": v(-20.83, -18.7) * mm});
            skLineSegment(sketch, "E151.MirrorCS", {"start": v(-14.5, -13.78) * mm, "end": v(-20.15, -19.44) * mm});
            skLineSegment(sketch, "E152.MirrorCS", {"start": v(-13.04, -15.16) * mm, "end": v(-18.7, -20.83) * mm});
            skArc(sketch, "E153.MirrorCS", {"start": v(13.04, 15.16) * mm, "mid": v(13.42, 14.83) * mm, "end": v(13.78, 14.5) * mm});
            skArc(sketch, "E154.MirrorCS", {"start": v(14.5, 13.78) * mm, "mid": v(14.83, 13.42) * mm, "end": v(15.16, 13.04) * mm});
            skArc(sketch, "E155.MirrorCS", {"start": v(18.7, 20.83) * mm, "mid": v(19.08, 20.5) * mm, "end": v(19.44, 20.15) * mm});
            skArc(sketch, "E156.MirrorCS", {"start": v(20.15, 19.44) * mm, "mid": v(20.5, 19.08) * mm, "end": v(20.83, 18.7) * mm});
            skLineSegment(sketch, "E157.MirrorCS", {"start": v(13.04, 15.16) * mm, "end": v(18.7, 20.83) * mm});
            skLineSegment(sketch, "E158.MirrorCS", {"start": v(14.5, 13.78) * mm, "end": v(20.15, 19.44) * mm});
            skLineSegment(sketch, "E159.MirrorCS", {"start": v(13.78, 14.5) * mm, "end": v(19.44, 20.15) * mm});
            skPoint(sketch, "E160.MirrorP", {"position": v(13.04, 15.16) * mm});
            skLineSegment(sketch, "E161.MirrorCS", {"start": v(15.16, 13.04) * mm, "end": v(20.83, 18.7) * mm});
            skArc(sketch, "E162.MirrorCS", {"start": v(13.04, -15.16) * mm, "mid": v(13.42, -14.83) * mm, "end": v(13.78, -14.5) * mm});
            skArc(sketch, "E163.MirrorCS", {"start": v(14.5, -13.78) * mm, "mid": v(14.83, -13.42) * mm, "end": v(15.16, -13.04) * mm});
            skArc(sketch, "E164.MirrorCS", {"start": v(18.7, -20.83) * mm, "mid": v(19.08, -20.5) * mm, "end": v(19.44, -20.15) * mm});
            skArc(sketch, "E165.MirrorCS", {"start": v(20.15, -19.44) * mm, "mid": v(20.5, -19.08) * mm, "end": v(20.83, -18.7) * mm});
            skLineSegment(sketch, "E166.MirrorCS", {"start": v(14.5, -13.78) * mm, "end": v(20.15, -19.44) * mm});
            skPoint(sketch, "E167.MirrorP", {"position": v(13.04, -15.16) * mm});
            skLineSegment(sketch, "E168.MirrorCS", {"start": v(13.04, -15.16) * mm, "end": v(18.7, -20.83) * mm});
            skLineSegment(sketch, "E169.MirrorCS", {"start": v(13.78, -14.5) * mm, "end": v(19.44, -20.15) * mm});
            skLineSegment(sketch, "E170.MirrorCS", {"start": v(15.16, -13.04) * mm, "end": v(20.83, -18.7) * mm});
            skSolve(sketch);
        }
        {
            var Q0;
            Q0=qSketchRegion(id+"F8",true);
            extrude(context, id + "F9", {"entities" : qUnion([Q0]), "operationType" : NewBodyOperationType.REMOVE, "oppositeDirection" : true, "depth" : 25 * mm, "offsetDistance" : 25 * mm});
        }
        {
            var Q0;
            Q0=qCreatedBy(makeId("Top.planeOp"),FACE);
            var sketch = newSketch(context, id + "F10", { "sketchPlane" : qUnion([Q0])});
            skArc(sketch, "E171", {"start": v(-24.68, 21.15) * mm, "mid": v(-30.03, 12.44) * mm, "end": v(-32.4, 2.5) * mm});
            skCircle(sketch, "E172.0", {"center": v(0, 0) * mm, "radius": 34.5 * mm});
            skLineSegment(sketch, "E173", {"start": v(-37.67, 0) * mm, "end": v(46.27, 0) * mm, "construction": true});
            skArc(sketch, "E174", {"start": v(-22.9, 19.37) * mm, "mid": v(-27.72, 11.48) * mm, "end": v(-29.9, 2.5) * mm});
            skLineSegment(sketch, "E175", {"start": v(-29.9, 2.5) * mm, "end": v(-32.4, 2.5) * mm});
            skLineSegment(sketch, "E176", {"start": v(-29.9, -2.5) * mm, "end": v(-32.4, -2.5) * mm});
            skLineSegment(sketch, "E177", {"start": v(0, 36.71) * mm, "end": v(0, -36.92) * mm, "construction": true});
            skLineSegment(sketch, "E178", {"start": v(0, 0) * mm, "end": v(-28.2, 28.2) * mm, "construction": true});
            skLineSegment(sketch, "E179", {"start": v(-22.9, 19.37) * mm, "end": v(-24.68, 21.15) * mm});
            skLineSegment(sketch, "E180", {"start": v(-19.37, 22.9) * mm, "end": v(-21.15, 24.68) * mm});
            skLineSegment(sketch, "E181.MirrorCS", {"start": v(-22.9, -19.37) * mm, "end": v(-24.68, -21.15) * mm});
            skLineSegment(sketch, "E182.MirrorCS", {"start": v(-19.37, -22.9) * mm, "end": v(-21.15, -24.68) * mm});
            skLineSegment(sketch, "E183.MirrorCS", {"start": v(19.37, 22.9) * mm, "end": v(21.15, 24.68) * mm});
            skLineSegment(sketch, "E184.MirrorCS", {"start": v(22.9, 19.37) * mm, "end": v(24.68, 21.15) * mm});
            skLineSegment(sketch, "E185.MirrorCS", {"start": v(29.9, 2.5) * mm, "end": v(32.4, 2.5) * mm});
            skLineSegment(sketch, "E186.MirrorCS", {"start": v(29.9, -2.5) * mm, "end": v(32.4, -2.5) * mm});
            skLineSegment(sketch, "E187.MirrorCS", {"start": v(22.9, -19.37) * mm, "end": v(24.68, -21.15) * mm});
            skLineSegment(sketch, "E188.MirrorCS", {"start": v(19.37, -22.9) * mm, "end": v(21.15, -24.68) * mm});
            skArc(sketch, "E189.trimOffspring", {"start": v(-29.9, -2.5) * mm, "mid": v(-27.72, -11.48) * mm, "end": v(-22.9, -19.37) * mm});
            skArc(sketch, "E190.trimOffspring", {"start": v(-32.4, -2.5) * mm, "mid": v(-30.03, -12.44) * mm, "end": v(-24.68, -21.15) * mm});
            skArc(sketch, "E191.trimOffspring", {"start": v(-19.37, -22.9) * mm, "mid": v(-13.78, -26.65) * mm, "end": v(-7.5, -29.05) * mm});
            skArc(sketch, "E192.trimOffspring", {"start": v(-21.15, -24.68) * mm, "mid": v(-14.74, -28.97) * mm, "end": v(-7.5, -31.62) * mm});
            skArc(sketch, "E193.trimOffspring", {"start": v(22.9, -19.37) * mm, "mid": v(27.72, -11.48) * mm, "end": v(29.9, -2.5) * mm});
            skArc(sketch, "E194.trimOffspring", {"start": v(24.68, -21.15) * mm, "mid": v(30.03, -12.44) * mm, "end": v(32.4, -2.5) * mm});
            skArc(sketch, "E195.trimOffspring", {"start": v(29.9, 2.5) * mm, "mid": v(27.72, 11.48) * mm, "end": v(22.9, 19.37) * mm});
            skArc(sketch, "E196.trimOffspring", {"start": v(32.4, 2.5) * mm, "mid": v(30.03, 12.44) * mm, "end": v(24.68, 21.15) * mm});
            skArc(sketch, "E197.trimOffspring", {"start": v(19.37, 22.9) * mm, "mid": v(11.02, 27.9) * mm, "end": v(1.5, 29.96) * mm});
            skArc(sketch, "E198.trimOffspring", {"start": v(21.15, 24.68) * mm, "mid": v(11.97, 30.21) * mm, "end": v(1.5, 32.47) * mm});
            skCircle(sketch, "E199", {"center": v(0, 0) * mm, "radius": 28 * mm});
            skLineSegment(sketch, "E200", {"start": v(-1.5, 29.96) * mm, "end": v(-1.5, 32.47) * mm});
            skLineSegment(sketch, "E201", {"start": v(1.5, 29.96) * mm, "end": v(1.5, 32.47) * mm});
            skLineSegment(sketch, "E202", {"start": v(-7.5, -29.05) * mm, "end": v(-7.5, -31.62) * mm});
            skLineSegment(sketch, "E203", {"start": v(7.5, -29.05) * mm, "end": v(7.5, -31.62) * mm});
            skArc(sketch, "E204.trimOffspring", {"start": v(7.5, -29.05) * mm, "mid": v(13.78, -26.65) * mm, "end": v(19.37, -22.9) * mm});
            skArc(sketch, "E205.trimOffspring", {"start": v(7.5, -31.62) * mm, "mid": v(14.74, -28.97) * mm, "end": v(21.15, -24.68) * mm});
            skArc(sketch, "E206.trimOffspring", {"start": v(-1.5, 32.47) * mm, "mid": v(-11.97, 30.21) * mm, "end": v(-21.15, 24.68) * mm});
            skArc(sketch, "E207.trimOffspring", {"start": v(-1.5, 29.96) * mm, "mid": v(-11.02, 27.9) * mm, "end": v(-19.37, 22.9) * mm});
            skSolve(sketch);
        }
        {
            var Q0;
            Q0 = qSketchRegion(id + "F10", true);
            extrude(context, id + "F11", {"entities" : qUnion([Q0]), "operationType" : NewBodyOperationType.ADD, "depth" : 2 * mm, "offsetDistance" : 25 * mm});
        }
    });
